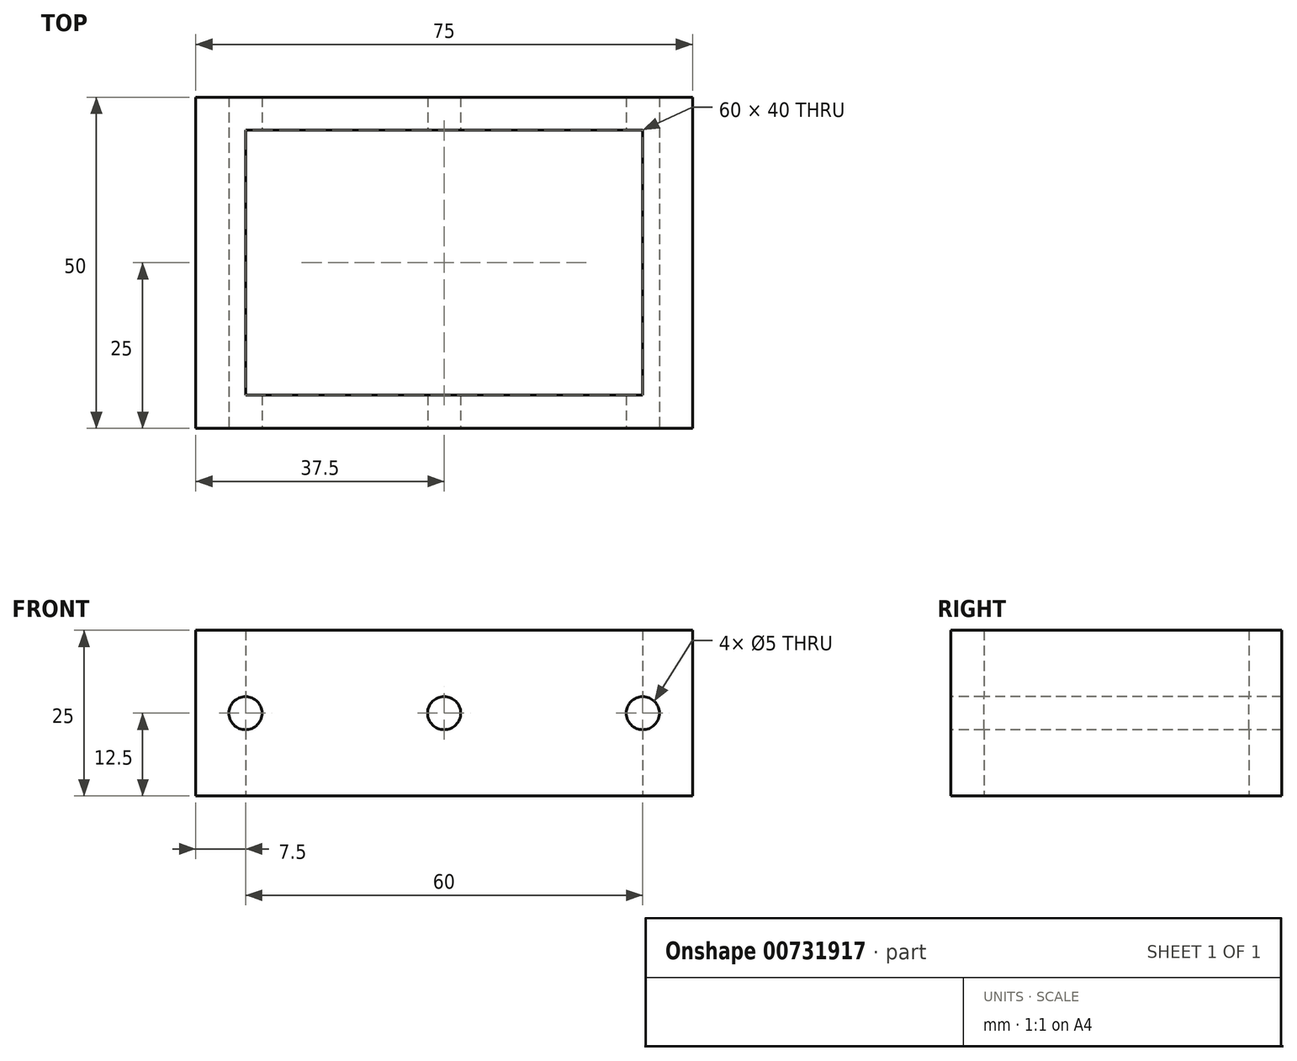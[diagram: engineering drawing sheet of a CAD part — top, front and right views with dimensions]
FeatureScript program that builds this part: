
annotation { "Feature Type Name" : "Feature", "Feature Type Description" : "" }
export const myFeature = defineFeature(function(context is Context, id is Id, definition is map)
    precondition{}
    {
        {
            var Q0;
            Q0=qCreatedBy(makeId("Top.planeOp"),FACE);
            var sketch = newSketch(context, id + "F0", { "sketchPlane" : qUnion([Q0])});
            skLineSegment(sketch, "E0.bottom", {"start": v(37.5, -25) * mm, "end": v(-37.5, -25) * mm});
            skLineSegment(sketch, "E0.top", {"start": v(37.5, 25) * mm, "end": v(-37.5, 25) * mm});
            skLineSegment(sketch, "E0.left", {"start": v(37.5, -25) * mm, "end": v(37.5, 25) * mm});
            skLineSegment(sketch, "E0.right", {"start": v(-37.5, -25) * mm, "end": v(-37.5, 25) * mm});
            skPoint(sketch, "E0.middle", {"position": v(0, 0) * mm});
            skLineSegment(sketch, "E1.bottom", {"start": v(30, -20) * mm, "end": v(-30, -20) * mm});
            skLineSegment(sketch, "E1.top", {"start": v(30, 20) * mm, "end": v(-30, 20) * mm});
            skLineSegment(sketch, "E1.left", {"start": v(30, -20) * mm, "end": v(30, 20) * mm});
            skLineSegment(sketch, "E1.right", {"start": v(-30, -20) * mm, "end": v(-30, 20) * mm});
            skSolve(sketch);
        }
        {
            var Q0;
            Q0=qSketchRegion(id+"F0",true);
            extrude(context, id + "F1", {"entities" : qUnion([Q0]), "endBound" : BoundingType.SYMMETRIC, "depth" : 25 * mm, "offsetDistance" : 25.4 * mm});
        }
        {
            var Q0;
            Q0=qCreatedBy(makeId("Front.planeOp"),FACE);
            var sketch = newSketch(context, id + "F2", { "sketchPlane" : qUnion([Q0])});
            skCircle(sketch, "E2", {"center": v(-30, 0) * mm, "radius": 2.5 * mm});
            skCircle(sketch, "E3", {"center": v(30, 0) * mm, "radius": 2.5 * mm});
            skCircle(sketch, "E4", {"center": v(0, 0) * mm, "radius": 2.5 * mm});
            skSolve(sketch);
        }
        {
            var Q0;
            Q0=qSketchRegion(id+"F2",true);
            extrude(context, id + "F3", {"entities" : qUnion([Q0]), "operationType" : NewBodyOperationType.REMOVE, "endBound" : BoundingType.THROUGH_ALL, "oppositeDirection" : true, "depth" : 25.4 * mm, "offsetDistance" : 25.4 * mm, "hasSecondDirection" : true, "secondDirectionBound" : SecondDirectionBoundingType.THROUGH_ALL, "secondDirectionOppositeDirection" : false, "secondDirectionDepth" : 25.4 * mm});
        }
    });
